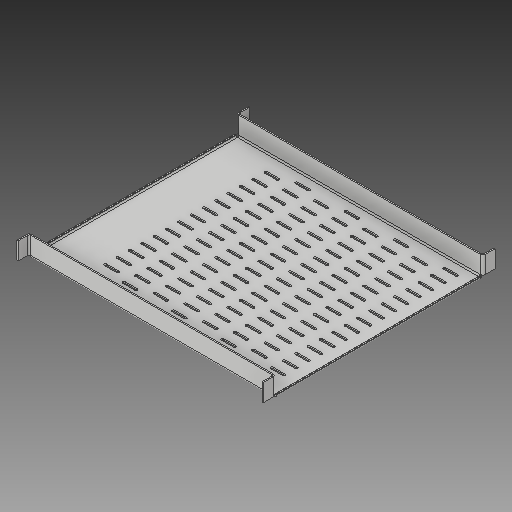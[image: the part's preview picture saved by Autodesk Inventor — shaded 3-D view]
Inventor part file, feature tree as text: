
AUTODESK INVENTOR PART (.ipt)
format: ipt  version: 2017 (Build 210142000, 142)  size: 569,856 bytes
history: native  units: in
note: dims shown in document units (in); Inventor stores cm internally (conversion verified against a paired STEP export)
features: sheet_metal_op x10, sketch x5, other x4, extrude x1, pattern_linear x1
ambient origin geometry x8: Origin, YZ Plane, XZ Plane, XY Plane, X Axis, Y Axis, Z Axis, Center Point
bodies: Solid1 (feature_tree)
feature tree (21):
  sheet_metal_op  "Face1"
  sheet_metal_op  "Flange1"
  sheet_metal_op  "Flange2"
  sheet_metal_op  "Flange3"
  extrude  "Extrusion1"  Depth=17.0in
  pattern_linear  "Rectangular Pattern1"  Spacing1=0.1046in  [1 undecoded]
  sketch  "Sketch1"  dims[d0=20.0in d1=17.0in]
  other  "Plate1"
  sketch  "Sketch2"  dims[d2=0.1046in]
  other  "Plate2"
  sheet_metal_op  "Bend1"
  sheet_metal_op  "Corner1"
  sketch  "Sketch3"  dims[d3=0.1046in]
  other  "Plate3"
  sheet_metal_op  "Bend2"
  sheet_metal_op  "Corner2"
  sketch  "Sketch4"  dims[d4=0.0523in]
  other  "Plate4"
  sheet_metal_op  "Bend3"
  sheet_metal_op  "Corner3"
  sketch  "Sketch5"  dims[d5=0.2092in d6=0.1046in d7=1.625in d8=90.0deg d9=0.1046in d10=0.4184in d11=0.1046in d12=0.1046in d13=0.1046in d14=0.0523in d15=0.2092in d16=0.1046in d17=1.0in d18=90.0deg d19=0.1046in d20=0.4184in d21=0.1046in d22=0.1046in d23=0.1046in d24=0.0523in d25=0.2092in d26=0.1046in d27=0.25in d28=90.0deg d29=0.1046in d30=0.4184in d31=0.1046in d32=0.1046in d33=1.0in d34=1.0in d35=0.7in d36=1.2in d37=3.0in d38=0.2in d39=0.2in d40=1.0in d41=1.0in d42=0.0in d43=6.2992in d45=1.0in d46=1.5748in d48=4.0in]
note: 1 required parameter value undecoded (feature->parameter linkage not recoverable at this tier; creation-order binding heuristic only, values carry confidence <= 0.55)
